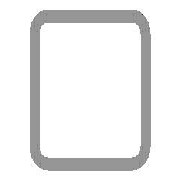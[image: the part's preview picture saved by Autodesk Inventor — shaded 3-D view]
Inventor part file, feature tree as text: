
AUTODESK INVENTOR PART (.ipt)
format: ipt  version: 2025.3 (Build 293356030, 356C)  size: 151,040 bytes
history: native  units: mm (DEFAULTED — no unit token found)
features: other x4, plane x3, split x2, sketch x1
ambient origin geometry x8: Origin, YZ Plane, XZ Plane, XY Plane, X Axis, Y Axis, Z Axis, Center Point
bodies: Solid1 (feature_tree), Body (feature_tree)
feature tree (10):
  parser-record x1  (decoder bookkeeping rows leaked as tree rows — omitted from the tree; the rows remain in map.json)
  other  "Driven Length"
  other  "Start Plane"
  other  "End Plane"
  plane  "Work Plane4"
  split  "Split1"
  plane  "Work Plane5"
  split  "Split2"
  sketch  "Sketch3"  dims[d3=753.362526mm d4=0.0mm d7=4.0mm d9=40.0mm d11=40.0mm d12=2.0mm d13=190.506469mm d14=943.868995mm d15=20.0mm d16=20.0mm d17=90.0deg d18=753.362526mm]
  plane  "Work Plane3"
